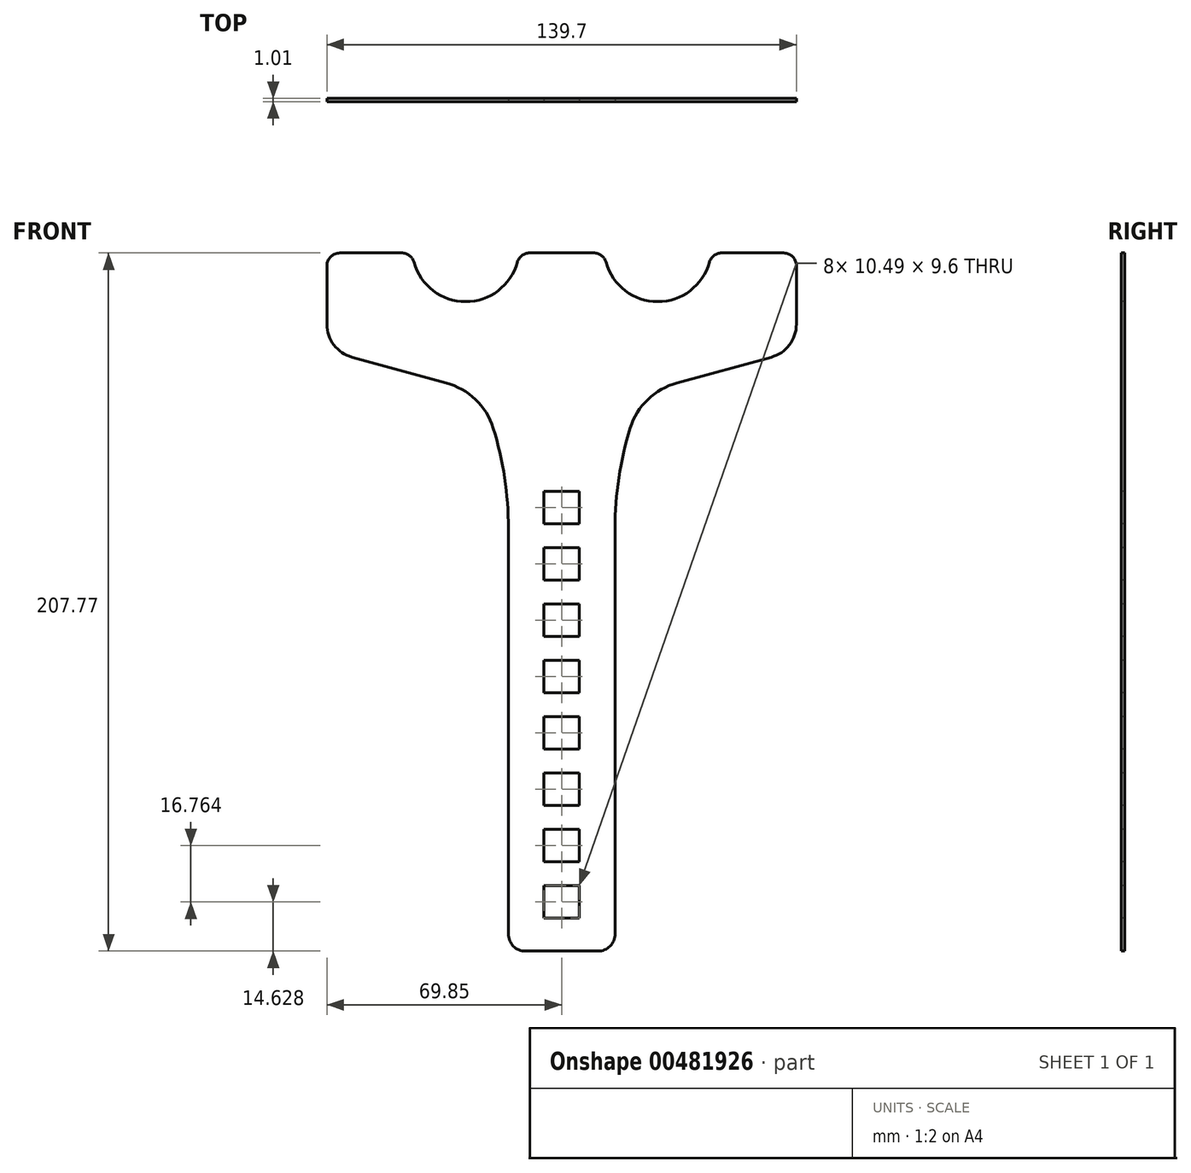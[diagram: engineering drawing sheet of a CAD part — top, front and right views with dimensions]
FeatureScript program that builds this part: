
annotation { "Feature Type Name" : "Feature", "Feature Type Description" : "" }
export const myFeature = defineFeature(function(context is Context, id is Id, definition is map)
    precondition{}
    {
        {
            var Q0;
            Q0=qCreatedBy(makeId("Front.planeOp"),FACE);
            var sketch = newSketch(context, id + "F0", { "sketchPlane" : qUnion([Q0])});
            skPoint(sketch, "E0.middle", {"position": v(0, 0) * mm});
            skLineSegment(sketch, "E1", {"start": v(-69.85, 0) * mm, "end": v(69.85, 0) * mm});
            skLineSegment(sketch, "E2", {"start": v(-69.85, 0) * mm, "end": v(-69.85, -28.96) * mm});
            skLineSegment(sketch, "E3.MirrorCS", {"start": v(69.85, 0) * mm, "end": v(69.85, -28.96) * mm});
            skPoint(sketch, "E4.middle", {"position": v(0, -50.17) * mm});
            skLineSegment(sketch, "E5", {"start": v(-69.85, -28.96) * mm, "end": v(-15.87, -28.96) * mm, "construction": true});
            skLineSegment(sketch, "E6", {"start": v(-69.85, -28.96) * mm, "end": v(-23.72, -41.59) * mm});
            skLineSegment(sketch, "E7", {"start": v(-23.72, -41.59) * mm, "end": v(-15.87, -66.22) * mm});
            skLineSegment(sketch, "E8", {"start": v(-15.87, -66.22) * mm, "end": v(-15.87, -207.77) * mm});
            skLineSegment(sketch, "E9", {"start": v(-15.87, -207.77) * mm, "end": v(0, -207.77) * mm});
            skLineSegment(sketch, "E10.MirrorCS", {"start": v(69.85, -28.96) * mm, "end": v(23.72, -41.59) * mm});
            skLineSegment(sketch, "E11.MirrorCS", {"start": v(23.72, -41.59) * mm, "end": v(15.87, -66.22) * mm});
            skLineSegment(sketch, "E12.MirrorCS", {"start": v(15.87, -66.22) * mm, "end": v(15.87, -207.77) * mm});
            skLineSegment(sketch, "E13.MirrorCS", {"start": v(15.87, -207.77) * mm, "end": v(0, -207.77) * mm});
            skLineSegment(sketch, "E14", {"start": v(-69.85, 0) * mm, "end": v(-44.45, 0) * mm, "construction": true});
            skLineSegment(sketch, "E15", {"start": v(-44.45, 0) * mm, "end": v(-12.7, 0) * mm, "construction": true});
            skLineSegment(sketch, "E16", {"start": v(-28.58, 0) * mm, "end": v(-28.58, -14.48) * mm, "construction": true});
            skArc(sketch, "E17", {"start": v(-44.45, 0) * mm, "mid": v(-28.58, -14.48) * mm, "end": v(-12.7, 0) * mm});
            skArc(sketch, "E18.MirrorCS", {"start": v(44.45, 0) * mm, "mid": v(28.58, -14.48) * mm, "end": v(12.7, 0) * mm});
            skLineSegment(sketch, "E19", {"start": v(0, 0) * mm, "end": v(0, -92.56) * mm, "construction": true});
            skLineSegment(sketch, "E20.bottom", {"start": v(5.25, -97.36) * mm, "end": v(-5.25, -97.36) * mm});
            skLineSegment(sketch, "E20.top", {"start": v(5.25, -87.76) * mm, "end": v(-5.25, -87.76) * mm});
            skLineSegment(sketch, "E20.left", {"start": v(5.25, -97.36) * mm, "end": v(5.25, -87.76) * mm});
            skLineSegment(sketch, "E20.right", {"start": v(-5.25, -97.36) * mm, "end": v(-5.25, -87.76) * mm});
            skPoint(sketch, "E20.middle", {"position": v(0, -92.56) * mm});
            skLineSegment(sketch, "E21", {"start": v(-5.25, -97.36) * mm, "end": v(-5.25, -104.52) * mm, "construction": true});
            skLineSegment(sketch, "E22", {"start": v(-5.25, -104.52) * mm, "end": v(-5.25, -114.12) * mm, "construction": true});
            skLineSegment(sketch, "E23", {"start": v(-5.25, -114.12) * mm, "end": v(-5.25, -121.29) * mm, "construction": true});
            skLineSegment(sketch, "E24", {"start": v(-5.25, -121.29) * mm, "end": v(-5.25, -130.89) * mm, "construction": true});
            skLineSegment(sketch, "E25", {"start": v(-5.25, -130.89) * mm, "end": v(-5.25, -138.05) * mm, "construction": true});
            skLineSegment(sketch, "E26", {"start": v(-5.25, -138.05) * mm, "end": v(-5.25, -147.65) * mm, "construction": true});
            skLineSegment(sketch, "E27", {"start": v(-5.25, -147.65) * mm, "end": v(-5.25, -154.81) * mm, "construction": true});
            skLineSegment(sketch, "E28", {"start": v(-5.25, -154.81) * mm, "end": v(-5.25, -164.41) * mm, "construction": true});
            skLineSegment(sketch, "E29", {"start": v(-5.25, -164.41) * mm, "end": v(-5.25, -171.58) * mm, "construction": true});
            skLineSegment(sketch, "E30", {"start": v(-5.25, -171.58) * mm, "end": v(-5.25, -181.18) * mm, "construction": true});
            skLineSegment(sketch, "E31.bottom", {"start": v(-5.25, -104.52) * mm, "end": v(5.25, -104.52) * mm});
            skLineSegment(sketch, "E31.top", {"start": v(-5.25, -114.12) * mm, "end": v(5.25, -114.12) * mm});
            skLineSegment(sketch, "E31.left", {"start": v(-5.25, -104.52) * mm, "end": v(-5.25, -114.12) * mm});
            skLineSegment(sketch, "E31.right", {"start": v(5.25, -104.52) * mm, "end": v(5.25, -114.12) * mm});
            skLineSegment(sketch, "E32.bottom", {"start": v(-5.25, -121.29) * mm, "end": v(5.25, -121.29) * mm});
            skLineSegment(sketch, "E32.top", {"start": v(-5.25, -130.89) * mm, "end": v(5.25, -130.89) * mm});
            skLineSegment(sketch, "E32.left", {"start": v(-5.25, -121.29) * mm, "end": v(-5.25, -130.89) * mm});
            skLineSegment(sketch, "E32.right", {"start": v(5.25, -121.29) * mm, "end": v(5.25, -130.89) * mm});
            skLineSegment(sketch, "E33.bottom", {"start": v(-5.25, -138.05) * mm, "end": v(5.25, -138.05) * mm});
            skLineSegment(sketch, "E33.top", {"start": v(-5.25, -147.65) * mm, "end": v(5.25, -147.65) * mm});
            skLineSegment(sketch, "E33.left", {"start": v(-5.25, -138.05) * mm, "end": v(-5.25, -147.65) * mm});
            skLineSegment(sketch, "E33.right", {"start": v(5.25, -138.05) * mm, "end": v(5.25, -147.65) * mm});
            skLineSegment(sketch, "E34.bottom", {"start": v(-5.25, -154.81) * mm, "end": v(5.25, -154.81) * mm});
            skLineSegment(sketch, "E34.top", {"start": v(-5.25, -164.41) * mm, "end": v(5.25, -164.41) * mm});
            skLineSegment(sketch, "E34.left", {"start": v(-5.25, -154.81) * mm, "end": v(-5.25, -164.41) * mm});
            skLineSegment(sketch, "E34.right", {"start": v(5.25, -154.81) * mm, "end": v(5.25, -164.41) * mm});
            skLineSegment(sketch, "E35.bottom", {"start": v(-5.25, -171.58) * mm, "end": v(5.25, -171.58) * mm});
            skLineSegment(sketch, "E35.top", {"start": v(-5.25, -181.18) * mm, "end": v(5.25, -181.18) * mm});
            skLineSegment(sketch, "E35.left", {"start": v(-5.25, -171.58) * mm, "end": v(-5.25, -181.18) * mm});
            skLineSegment(sketch, "E35.right", {"start": v(5.25, -171.58) * mm, "end": v(5.25, -181.18) * mm});
            skLineSegment(sketch, "E36", {"start": v(-5.25, -181.18) * mm, "end": v(-5.25, -97.36) * mm});
            skLineSegment(sketch, "E37", {"start": v(-5.25, -87.76) * mm, "end": v(-5.25, -80.6) * mm, "construction": true});
            skLineSegment(sketch, "E38", {"start": v(-5.25, -80.6) * mm, "end": v(-5.25, -71) * mm, "construction": true});
            skLineSegment(sketch, "E39.bottom", {"start": v(-5.25, -71) * mm, "end": v(5.25, -71) * mm});
            skLineSegment(sketch, "E39.top", {"start": v(-5.25, -80.6) * mm, "end": v(5.25, -80.6) * mm});
            skLineSegment(sketch, "E39.left", {"start": v(-5.25, -71) * mm, "end": v(-5.25, -80.6) * mm});
            skLineSegment(sketch, "E39.right", {"start": v(5.25, -71) * mm, "end": v(5.25, -80.6) * mm});
            skLineSegment(sketch, "E40", {"start": v(0, 0) * mm, "end": v(0, -19.05) * mm, "construction": true});
            skLineSegment(sketch, "E41", {"start": v(0, -19.05) * mm, "end": v(62.5, -19.05) * mm, "construction": true});
            skLineSegment(sketch, "E42", {"start": v(28.58, -14.48) * mm, "end": v(28.58, -19.05) * mm, "construction": true});
            skLineSegment(sketch, "E43", {"start": v(28.58, -19.05) * mm, "end": v(28.58, -6.35) * mm, "construction": true});
            skLineSegment(sketch, "E44", {"start": v(-5.25, -181.18) * mm, "end": v(-5.25, -188.34) * mm, "construction": true});
            skLineSegment(sketch, "E45.bottom", {"start": v(-5.25, -188.34) * mm, "end": v(5.25, -188.34) * mm});
            skLineSegment(sketch, "E45.top", {"start": v(-5.25, -197.94) * mm, "end": v(5.25, -197.94) * mm});
            skLineSegment(sketch, "E45.left", {"start": v(-5.25, -188.34) * mm, "end": v(-5.25, -197.94) * mm});
            skLineSegment(sketch, "E45.right", {"start": v(5.25, -188.34) * mm, "end": v(5.25, -197.94) * mm});
            skSolve(sketch);
        }
        {
            var Q0;
            {var subQ6=sQuery(id+"F0.wireOp",EDGE,"E2");Q0=makeQuery(id+"F0.imprint","IMPRINT",FACE,{"disambiguationData":[TD([[makeQuery(id+"F0.imprint","IMPRINT",EDGE,{"derivedFrom":subQ6}),1.0]])]});}
            extrude(context, id + "F1", {"entities" : qUnion([Q0]), "oppositeDirection" : true, "depth" : 1 * mm, "offsetDistance" : 25.4 * mm});
        }
        {
            var Q0;
            Q0=makeQuery(id+"F1.opExtrude","SWEPT_EDGE",EDGE,{"disambiguationData":[OSD([sQuery(id+"F0.wireOp",EDGE,"E6"),sQuery(id+"F0.wireOp",EDGE,"E7")])]});
            var Q1;
            Q1=makeQuery(id+"F1.opExtrude","SWEPT_EDGE",EDGE,{"disambiguationData":[OSD([sQuery(id+"F0.wireOp",EDGE,"E10.MirrorCS"),sQuery(id+"F0.wireOp",EDGE,"E11.MirrorCS")])]});
            fillet(context, id + "F2", {"entities" : qUnion([Q0, Q1]), "radius" : 20.32 * mm, "tangentPropagation" : true, "allowEdgeOverflow" : false});
        }
        {
            var Q0;
            Q0=makeQuery(id+"F1.opExtrude","SWEPT_EDGE",EDGE,{"disambiguationData":[OSD([sQuery(id+"F0.wireOp",EDGE,"E2"),sQuery(id+"F0.wireOp",EDGE,"E6")])]});
            var Q1;
            Q1=makeQuery(id+"F1.opExtrude","SWEPT_EDGE",EDGE,{"disambiguationData":[OSD([sQuery(id+"F0.wireOp",EDGE,"E3.MirrorCS"),sQuery(id+"F0.wireOp",EDGE,"E10.MirrorCS")])]});
            fillet(context, id + "F3", {"entities" : qUnion([Q0, Q1]), "radius" : 10.16 * mm, "tangentPropagation" : true, "allowEdgeOverflow" : false});
        }
        {
            var Q0;
            Q0=makeQuery(id+"F1.opExtrude","SWEPT_EDGE",EDGE,{"disambiguationData":[OSD([sQuery(id+"F0.wireOp",EDGE,"E1"),sQuery(id+"F0.wireOp",EDGE,"E3.MirrorCS")])]});
            var Q1;
            Q1=makeQuery(id+"F1.opExtrude","SWEPT_EDGE",EDGE,{"disambiguationData":[OSD([sQuery(id+"F0.wireOp",EDGE,"E1"),sQuery(id+"F0.wireOp",EDGE,"E2")])]});
            fillet(context, id + "F4", {"entities" : qUnion([Q0, Q1]), "radius" : 3.8 * mm, "tangentPropagation" : true, "allowEdgeOverflow" : false});
        }
        {
            var Q0;
            {var subQ0=sQuery(id+"F0.wireOp",EDGE,"E18.MirrorCS");var subQ1=sQuery(id+"F0.wireOp",EDGE,"E1");Q0=makeQuery(id+"F1.opExtrude","SWEPT_EDGE",EDGE,{"disambiguationData":[OSD([subQ1,subQ0]),TDD([makeQuery(id+"F0.imprint","INTERSECT",VERTEX,{"disambiguationData":[OD(1.0)],"derivedFrom":[subQ1,subQ0]})])]});}
            var Q1;
            {var subQ0=sQuery(id+"F0.wireOp",EDGE,"E17");var subQ1=sQuery(id+"F0.wireOp",EDGE,"E1");Q1=makeQuery(id+"F1.opExtrude","SWEPT_EDGE",EDGE,{"disambiguationData":[OSD([subQ1,subQ0]),TDD([makeQuery(id+"F0.imprint","INTERSECT",VERTEX,{"disambiguationData":[OD(1.0)],"derivedFrom":[subQ1,subQ0]})])]});}
            var Q2;
            {var subQ0=sQuery(id+"F0.wireOp",EDGE,"E17");var subQ1=sQuery(id+"F0.wireOp",EDGE,"E1");Q2=makeQuery(id+"F1.opExtrude","SWEPT_EDGE",EDGE,{"disambiguationData":[OSD([subQ1,subQ0]),TDD([makeQuery(id+"F0.imprint","INTERSECT",VERTEX,{"disambiguationData":[OD(0.0)],"derivedFrom":[subQ1,subQ0]})])]});}
            var Q3;
            {var subQ0=sQuery(id+"F0.wireOp",EDGE,"E18.MirrorCS");var subQ1=sQuery(id+"F0.wireOp",EDGE,"E1");Q3=makeQuery(id+"F1.opExtrude","SWEPT_EDGE",EDGE,{"disambiguationData":[OSD([subQ1,subQ0]),TDD([makeQuery(id+"F0.imprint","INTERSECT",VERTEX,{"disambiguationData":[OD(0.0)],"derivedFrom":[subQ1,subQ0]})])]});}
            fillet(context, id + "F5", {"entities" : qUnion([Q0, Q1, Q2, Q3]), "radius" : 3.8 * mm, "tangentPropagation" : true, "allowEdgeOverflow" : false});
        }
        {
            var Q0;
            Q0=makeQuery(id+"F1.opExtrude","SWEPT_EDGE",EDGE,{"disambiguationData":[OSD([sQuery(id+"F0.wireOp",EDGE,"E11.MirrorCS"),sQuery(id+"F0.wireOp",EDGE,"E12.MirrorCS")])]});
            var Q1;
            Q1=makeQuery(id+"F1.opExtrude","SWEPT_EDGE",EDGE,{"disambiguationData":[OSD([sQuery(id+"F0.wireOp",EDGE,"E7"),sQuery(id+"F0.wireOp",EDGE,"E8")])]});
            fillet(context, id + "F6", {"entities" : qUnion([Q0, Q1]), "radius" : 101.6 * mm, "tangentPropagation" : true, "allowEdgeOverflow" : false});
        }
        {
            var Q0;
            Q0=makeQuery(id+"F1.opExtrude","SWEPT_EDGE",EDGE,{"disambiguationData":[OSD([sQuery(id+"F0.wireOp",EDGE,"E12.MirrorCS"),sQuery(id+"F0.wireOp",EDGE,"E13.MirrorCS")])]});
            var Q1;
            Q1=makeQuery(id+"F1.opExtrude","SWEPT_EDGE",EDGE,{"disambiguationData":[OSD([sQuery(id+"F0.wireOp",EDGE,"E8"),sQuery(id+"F0.wireOp",EDGE,"E9")])]});
            fillet(context, id + "F7", {"entities" : qUnion([Q0, Q1]), "radius" : 5.08 * mm, "tangentPropagation" : true, "allowEdgeOverflow" : false});
        }
    });
